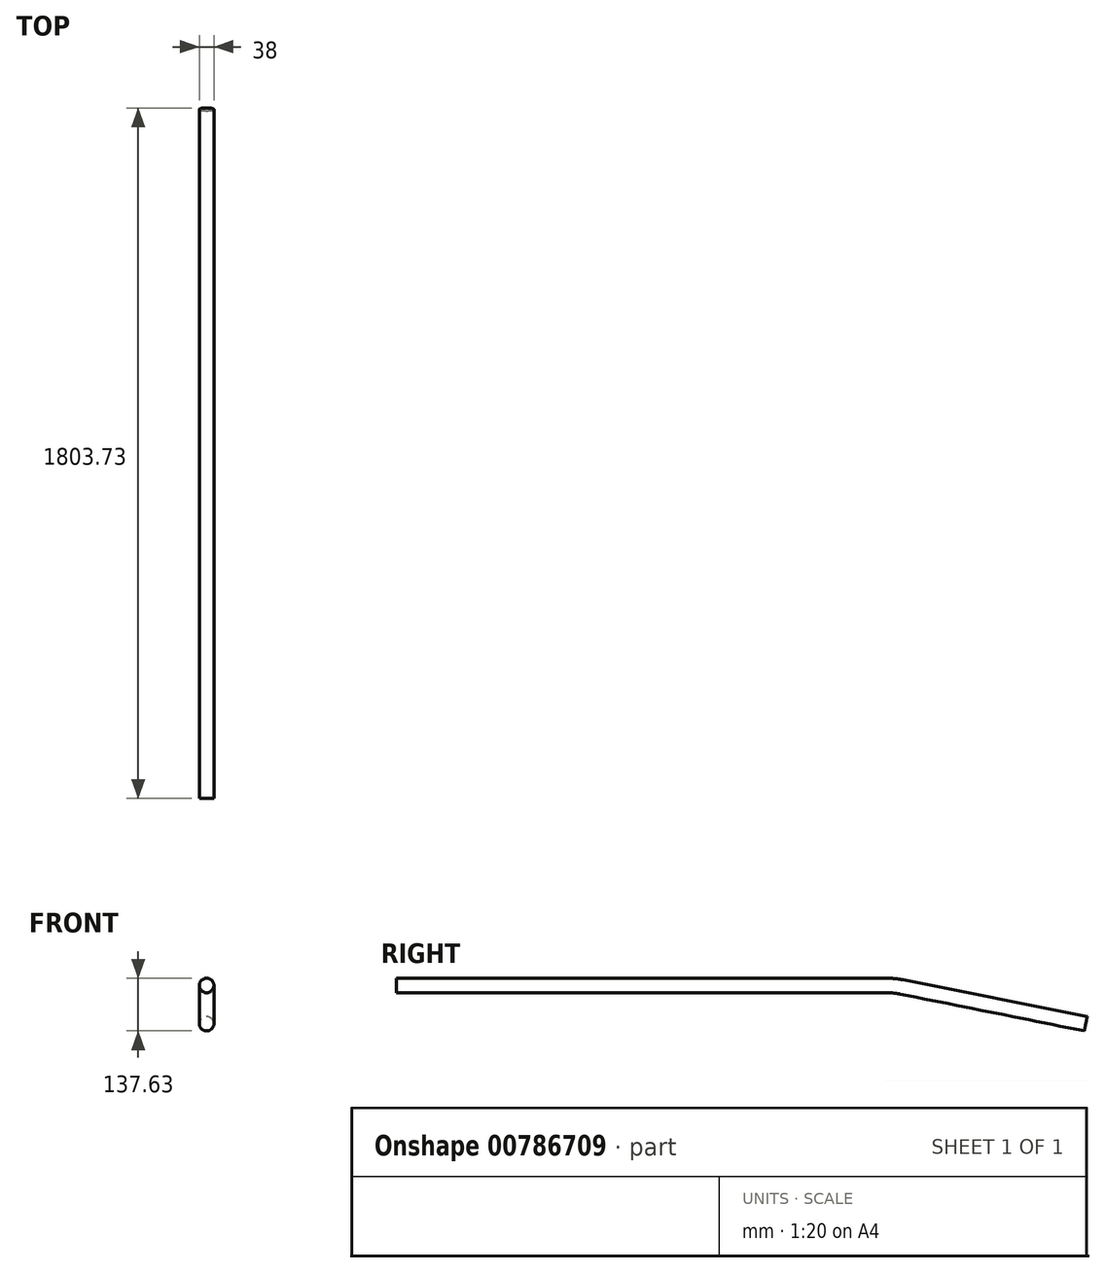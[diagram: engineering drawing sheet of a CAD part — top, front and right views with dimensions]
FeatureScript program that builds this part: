
annotation { "Feature Type Name" : "Feature", "Feature Type Description" : "" }
export const myFeature = defineFeature(function(context is Context, id is Id, definition is map)
    precondition{}
    {
        {
            var Q0;
            Q0=qCreatedBy(makeId("Right.planeOp"),FACE);
            var sketch = newSketch(context, id + "F0", { "sketchPlane" : qUnion([Q0])});
            skLineSegment(sketch, "E0", {"start": v(-914.83, 100) * mm, "end": v(365.36, 100) * mm});
            skLineSegment(sketch, "E1", {"start": v(-914.83, 100) * mm, "end": v(-914.83, 0) * mm, "construction": true});
            skLineSegment(sketch, "E2", {"start": v(404.59, 96.12) * mm, "end": v(885.17, 0) * mm});
            skPoint(sketch, "E3.visualSharp", {"position": v(385.17, 100) * mm});
            skArc(sketch, "E3.filletArc", {"start": v(404.59, 96.12) * mm, "mid": v(385.07, 99.03) * mm, "end": v(365.36, 100) * mm});
            skLineSegment(sketch, "E4", {"start": v(-914.83, 0) * mm, "end": v(885.17, 0) * mm, "construction": true});
            skSolve(sketch);
        }
        {
            var Q0;
            Q0=qCreatedBy(makeId("Front.planeOp"),FACE);
            var sketch = newSketch(context, id + "F1", { "sketchPlane" : qUnion([Q0])});
            skCircle(sketch, "E5", {"center": v(0, 100) * mm, "radius": 19 * mm});
            skSolve(sketch);
        }
        {
            var Q0;
            Q0 = qSketchRegion(id + "F1", true);
            var Q1;
            Q1 = qConstructionFilter(qBodyType(qCreatedBy(id + "F0" ,EDGE), BodyType.WIRE), ConstructionObject.NO);
            sweep(context, id + "F2", {"profiles" : qUnion([Q0]), "path" : qUnion([Q1])});
        }
    });
